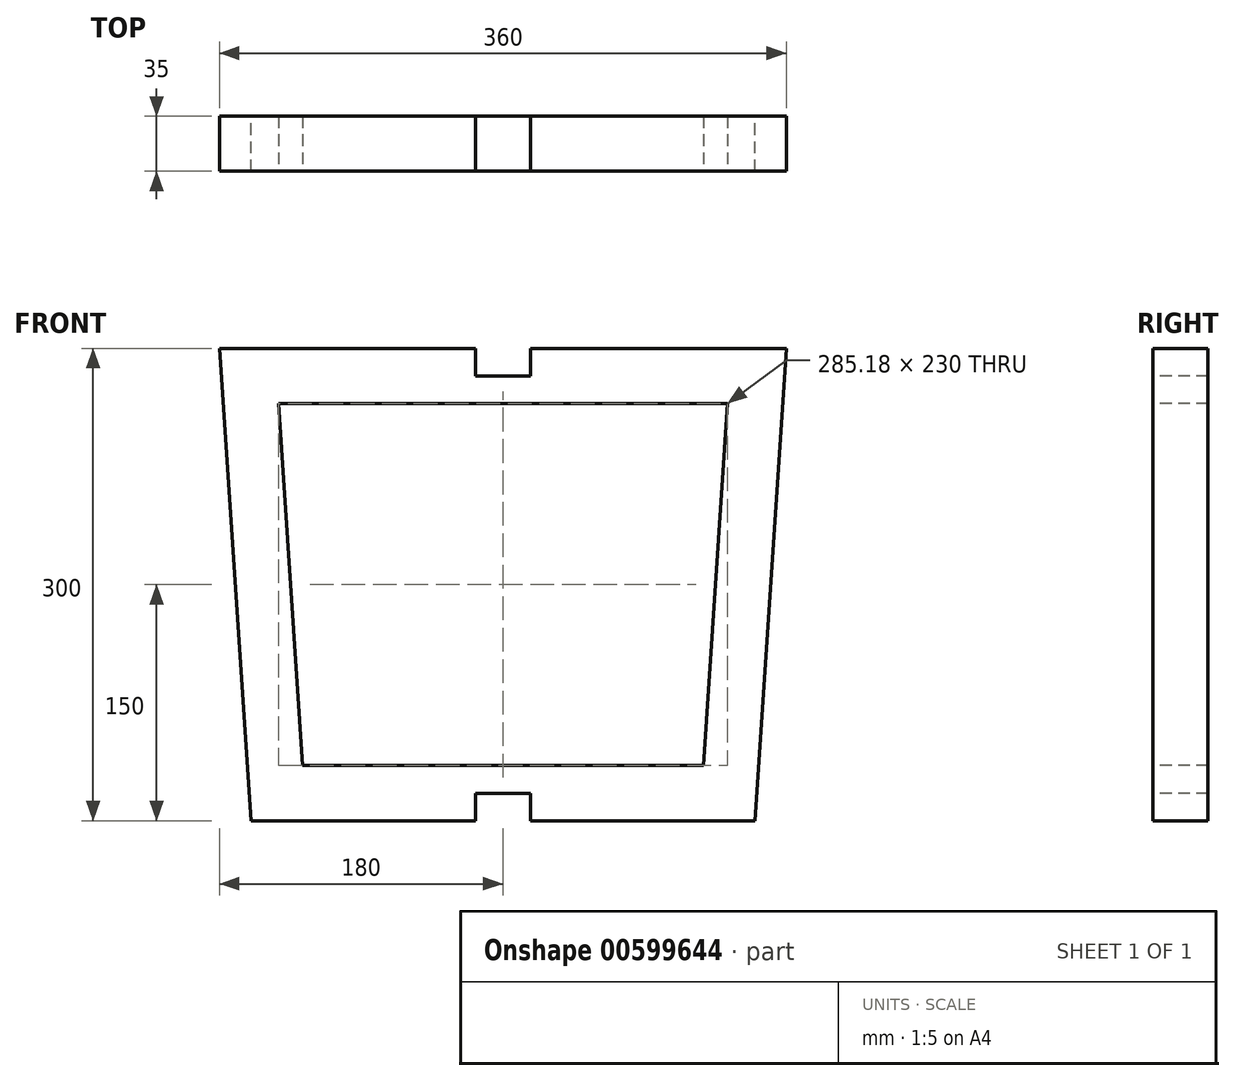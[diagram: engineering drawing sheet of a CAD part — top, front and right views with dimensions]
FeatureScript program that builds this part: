
annotation { "Feature Type Name" : "Feature", "Feature Type Description" : "" }
export const myFeature = defineFeature(function(context is Context, id is Id, definition is map)
    precondition{}
    {
        {
            var Q0;
            Q0=qCreatedBy(makeId("Front.planeOp"),FACE);
            var sketch = newSketch(context, id + "F0", { "sketchPlane" : qUnion([Q0])});
            skLineSegment(sketch, "E0", {"start": v(-180, 150) * mm, "end": v(180, 150) * mm});
            skLineSegment(sketch, "E1", {"start": v(180, 150) * mm, "end": v(160, -150) * mm});
            skLineSegment(sketch, "E2", {"start": v(160, -150) * mm, "end": v(-160, -150) * mm});
            skLineSegment(sketch, "E3", {"start": v(-160, -150) * mm, "end": v(-180, 150) * mm});
            skSolve(sketch);
        }
        {
            var Q0;
            Q0=makeQuery(id+"F0.imprint","IMPRINT",FACE,{"disambiguationData":[TD([[makeQuery(id+"F0.imprint","IMPRINT",EDGE,{"derivedFrom":sQuery(id+"F0.wireOp",EDGE,"E0")}),-1.0]])]});
            var sketch = newSketch(context, id + "F1", { "sketchPlane" : qUnion([Q0])});
            skLineSegment(sketch, "E4", {"start": v(-142.59, 115) * mm, "end": v(142.59, 115) * mm});
            skLineSegment(sketch, "E5", {"start": v(142.59, 115) * mm, "end": v(127.26, -115) * mm});
            skLineSegment(sketch, "E6", {"start": v(127.26, -115) * mm, "end": v(-127.26, -115) * mm});
            skLineSegment(sketch, "E7", {"start": v(-127.26, -115) * mm, "end": v(-142.59, 115) * mm});
            skSolve(sketch);
        }
        {
            var Q0;
            Q0=qSketchRegion(id+"F0",true);
            extrude(context, id + "F2", {"entities" : qUnion([Q0]), "endBound" : BoundingType.SYMMETRIC, "depth" : 35 * mm, "offsetDistance" : 25 * mm});
        }
        {
            var Q0;
            Q0=qSketchRegion(id+"F1",true);
            extrude(context, id + "F3", {"entities" : qUnion([Q0]), "operationType" : NewBodyOperationType.REMOVE, "endBound" : BoundingType.SYMMETRIC, "oppositeDirection" : true, "depth" : 35 * mm, "offsetDistance" : 25 * mm});
        }
        {
            var Q0;
            Q0=makeQuery(id+"F2.opExtrude","CAP_FACE",FACE,{"disambiguationData":[OSD([sQuery(id+"F0.wireOp",EDGE,"E0"),sQuery(id+"F0.wireOp",EDGE,"E1"),sQuery(id+"F0.wireOp",EDGE,"E2"),sQuery(id+"F0.wireOp",EDGE,"E3")])],"isStart":false});
            var sketch = newSketch(context, id + "F4", { "sketchPlane" : qUnion([Q0])});
            skLineSegment(sketch, "E8.bottom", {"start": v(-17.5, -150) * mm, "end": v(17.5, -150) * mm});
            skLineSegment(sketch, "E8.top", {"start": v(-17.5, -132.5) * mm, "end": v(17.5, -132.5) * mm});
            skLineSegment(sketch, "E8.left", {"start": v(-17.5, -150) * mm, "end": v(-17.5, -132.5) * mm});
            skLineSegment(sketch, "E8.right", {"start": v(17.5, -150) * mm, "end": v(17.5, -132.5) * mm});
            skSolve(sketch);
        }
        {
            var Q0;
            Q0 = qSketchRegion(id + "F4", true);
            extrude(context, id + "F5", {"entities" : qUnion([Q0]), "operationType" : NewBodyOperationType.REMOVE, "oppositeDirection" : true, "depth" : 35 * mm, "offsetDistance" : 25 * mm});
        }
        {
            var Q0;
            Q0=makeQuery(id+"F2.opExtrude","CAP_FACE",FACE,{"disambiguationData":[OSD([sQuery(id+"F0.wireOp",EDGE,"E0"),sQuery(id+"F0.wireOp",EDGE,"E1"),sQuery(id+"F0.wireOp",EDGE,"E2"),sQuery(id+"F0.wireOp",EDGE,"E3")])],"isStart":false});
            var sketch = newSketch(context, id + "F6", { "sketchPlane" : qUnion([Q0])});
            skLineSegment(sketch, "E9.bottom", {"start": v(-17.5, 150) * mm, "end": v(17.5, 150) * mm});
            skLineSegment(sketch, "E9.top", {"start": v(-17.5, 132.5) * mm, "end": v(17.5, 132.5) * mm});
            skLineSegment(sketch, "E9.left", {"start": v(-17.5, 150) * mm, "end": v(-17.5, 132.5) * mm});
            skLineSegment(sketch, "E9.right", {"start": v(17.5, 150) * mm, "end": v(17.5, 132.5) * mm});
            skSolve(sketch);
        }
        {
            var Q0;
            Q0 = qSketchRegion(id + "F6", true);
            extrude(context, id + "F7", {"entities" : qUnion([Q0]), "operationType" : NewBodyOperationType.REMOVE, "oppositeDirection" : true, "depth" : 35 * mm, "offsetDistance" : 25 * mm});
        }
    });
